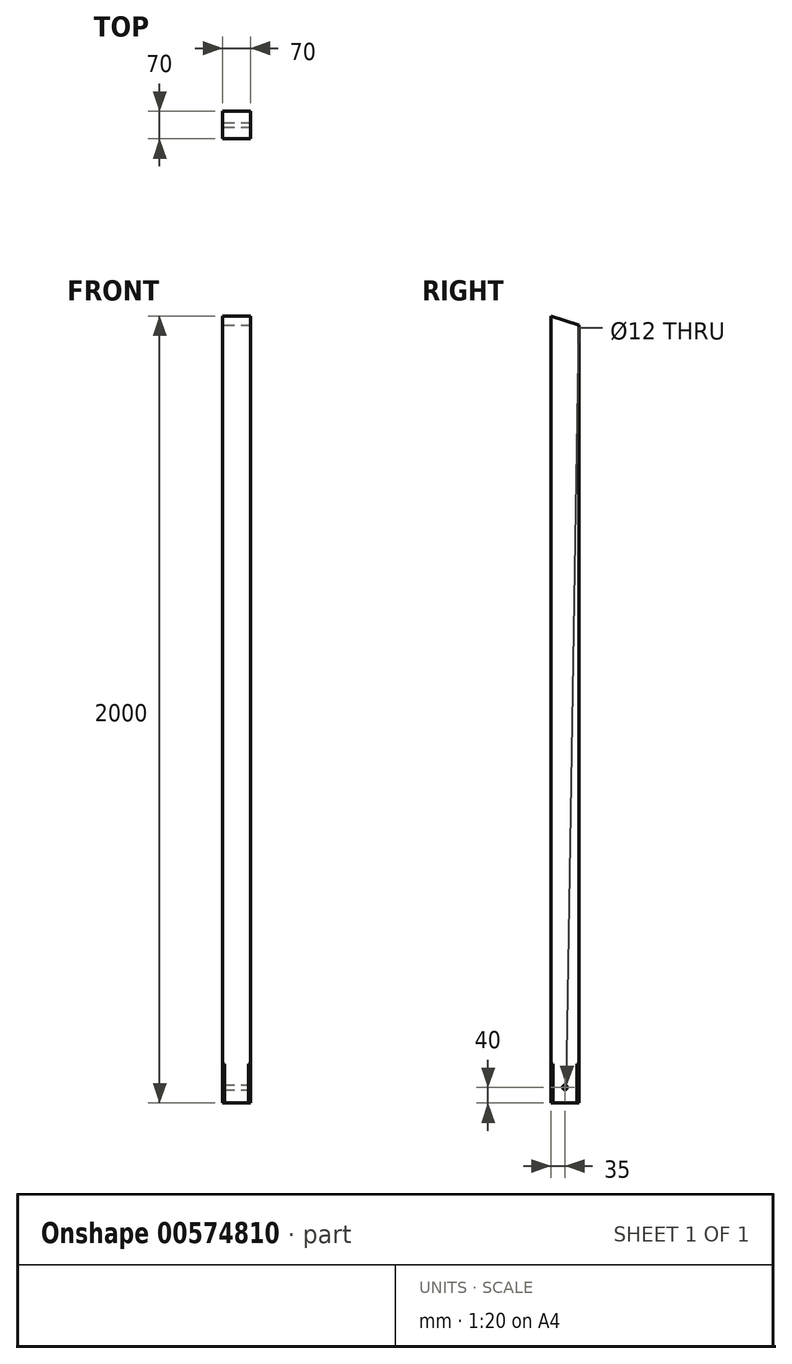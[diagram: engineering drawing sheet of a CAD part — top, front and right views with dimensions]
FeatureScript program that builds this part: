
annotation { "Feature Type Name" : "Feature", "Feature Type Description" : "" }
export const myFeature = defineFeature(function(context is Context, id is Id, definition is map)
    precondition{}
    {
        {
            var Q0;
            Q0=qCreatedBy(makeId("Top.planeOp"),FACE);
            var sketch = newSketch(context, id + "F0", { "sketchPlane" : qUnion([Q0])});
            skLineSegment(sketch, "E0.bottom", {"start": v(-35, -35) * mm, "end": v(35, -35) * mm});
            skLineSegment(sketch, "E0.top", {"start": v(-35, 35) * mm, "end": v(35, 35) * mm});
            skLineSegment(sketch, "E0.left", {"start": v(-35, -35) * mm, "end": v(-35, 35) * mm});
            skLineSegment(sketch, "E0.right", {"start": v(35, -35) * mm, "end": v(35, 35) * mm});
            skSolve(sketch);
        }
        {
            var Q0;
            Q0=makeQuery(id+"F0.imprint","IMPRINT",FACE,{"disambiguationData":[TD([[makeQuery(id+"F0.imprint","IMPRINT",EDGE,{"derivedFrom":sQuery(id+"F0.wireOp",EDGE,"E0.bottom")}),1.0]])]});
            extrude(context, id + "F1", {"entities" : qUnion([Q0]), "depth" : 100 * mm, "offsetDistance" : 25 * mm});
        }
        {
            var Q0;
            Q0=makeQuery(id+"F1.opExtrude","SWEPT_EDGE",EDGE,{"disambiguationData":[OSD([sQuery(id+"F0.wireOp",EDGE,"E0.bottom"),sQuery(id+"F0.wireOp",EDGE,"E0.left")])]});
            var Q1;
            Q1=makeQuery(id+"F1.opExtrude","SWEPT_EDGE",EDGE,{"disambiguationData":[OSD([sQuery(id+"F0.wireOp",EDGE,"E0.bottom"),sQuery(id+"F0.wireOp",EDGE,"E0.right")])]});
            var Q2;
            Q2=makeQuery(id+"F1.opExtrude","SWEPT_EDGE",EDGE,{"disambiguationData":[OSD([sQuery(id+"F0.wireOp",EDGE,"E0.top"),sQuery(id+"F0.wireOp",EDGE,"E0.right")])]});
            var Q3;
            Q3=makeQuery(id+"F1.opExtrude","SWEPT_EDGE",EDGE,{"disambiguationData":[OSD([sQuery(id+"F0.wireOp",EDGE,"E0.top"),sQuery(id+"F0.wireOp",EDGE,"E0.left")])]});
            chamfer(context, id + "F2", {"entities" : qUnion([Q0, Q1, Q2, Q3]), "width" : 5 * mm, "tangentPropagation" : true});
        }
        {
            var Q0;
            Q0=makeQuery(id+"F1.opExtrude","CAP_FACE",FACE,{"disambiguationData":[OSD([sQuery(id+"F0.wireOp",EDGE,"E0.bottom"),sQuery(id+"F0.wireOp",EDGE,"E0.top"),sQuery(id+"F0.wireOp",EDGE,"E0.left"),sQuery(id+"F0.wireOp",EDGE,"E0.right")])],"isStart":false});
            var sketch = newSketch(context, id + "F3", { "sketchPlane" : qUnion([Q0])});
            skLineSegment(sketch, "E1.bottom", {"start": v(35, 35) * mm, "end": v(-35, 35) * mm});
            skLineSegment(sketch, "E1.top", {"start": v(35, -35) * mm, "end": v(-35, -35) * mm});
            skLineSegment(sketch, "E1.left", {"start": v(35, 35) * mm, "end": v(35, -35) * mm});
            skLineSegment(sketch, "E1.right", {"start": v(-35, 35) * mm, "end": v(-35, -35) * mm});
            skSolve(sketch);
        }
        {
            var Q0;
            Q0 = qSketchRegion(id + "F3", true);
            extrude(context, id + "F4", {"entities" : qUnion([Q0]), "operationType" : NewBodyOperationType.ADD, "depth" : 1900 * mm, "offsetDistance" : 25 * mm});
        }
        {
            var Q0;
            Q0=makeQuery(id+"F4.boolean.opBoolean","MERGE",FACE,{"derivedFrom":[makeQuery(id+"F1.opExtrude","SWEPT_FACE",FACE,{"disambiguationData":[OSD([sQuery(id+"F0.wireOp",EDGE,"E0.right")])]}),makeQuery(id+"F4.opExtrude","SWEPT_FACE",FACE,{"disambiguationData":[OSD([sQuery(id+"F3.wireOp",EDGE,"E1.left")])]})]});
            var sketch = newSketch(context, id + "F5", { "sketchPlane" : qUnion([Q0])});
            skCircle(sketch, "E2", {"center": v(0, 40) * mm, "radius": 6 * mm});
            skLineSegment(sketch, "E3", {"start": v(-35, 2000) * mm, "end": v(35, 2000) * mm});
            skLineSegment(sketch, "E4", {"start": v(35, 2000) * mm, "end": v(35, 1976.67) * mm});
            skLineSegment(sketch, "E5", {"start": v(35, 1976.67) * mm, "end": v(-35, 2000) * mm});
            skSolve(sketch);
        }
        {
            var Q0;
            Q0 = qSketchRegion(id + "F5", true);
            extrude(context, id + "F6", {"entities" : qUnion([Q0]), "operationType" : NewBodyOperationType.REMOVE, "endBound" : BoundingType.THROUGH_ALL, "oppositeDirection" : true, "depth" : 25 * mm, "offsetDistance" : 25 * mm});
        }
    });
